# Revit family: Deckel_T-Abzweigstück_Russia
name_source: partatom
category: Generic Models
revit_build: Autodesk Revit 2015 (Build: 20140606_1530(x64)
units: mm (PartAtom-declared; Revit-internal decimal feet)

## types (7) — shared parameters
Manufacturer = OBO Bettermann
Material = Steel, Galvanized
URL = http://www.obo-bettermann.com

## per-type parameters (varying)
| type | A | D | GTIN | L | Manufacturer Art. No. |
| DFT 100 FS RU | 207 mm | 106 mm  [stored 0.347769 ft] | 4012196606412 | 311 mm  [stored 1.02034 ft] | 7128331 |
| DFT 150 FS RU | 257 mm | 106 mm  [stored 0.347769 ft] | 4012196649488 | 361 mm  [stored 1.18438 ft] | 7128332 |
| DFT 200 FS RU | 343 mm | 142 mm  [stored 0.465879 ft] | 4012196606429 | 481 mm  [stored 1.57808 ft] | 7128333 |
| DFT 300 FS RU | 443 mm | 142 mm  [stored 0.465879 ft] | 4012196606436 | 581 mm  [stored 1.90617 ft] | 7128335 |
| DFT 400 FS RU | 543 mm | 142 mm  [stored 0.465879 ft] | 4012196626441 | 681 mm  [stored 2.23425 ft] | 7128337 |
| DFT 500 FS RU | 643 mm | 142 mm  [stored 0.465879 ft] | 4012196626458 | 781 mm  [stored 2.56234 ft] | 7128339 |
| DFT 600 FS RU | 743 mm | 142 mm  [stored 0.465879 ft] | 4012196626465 | 881 mm  [stored 2.89042 ft] | 7128341 |

note: column(s) folded — value = type name in every type: Article Type

note: [stored X ft] marks values corroborated as IEEE doubles in the binary element streams (Revit-internal decimal feet)

## geometry (parser evidence)
native form markers: Sweep x2
no freeform markers — native parametric forms only
